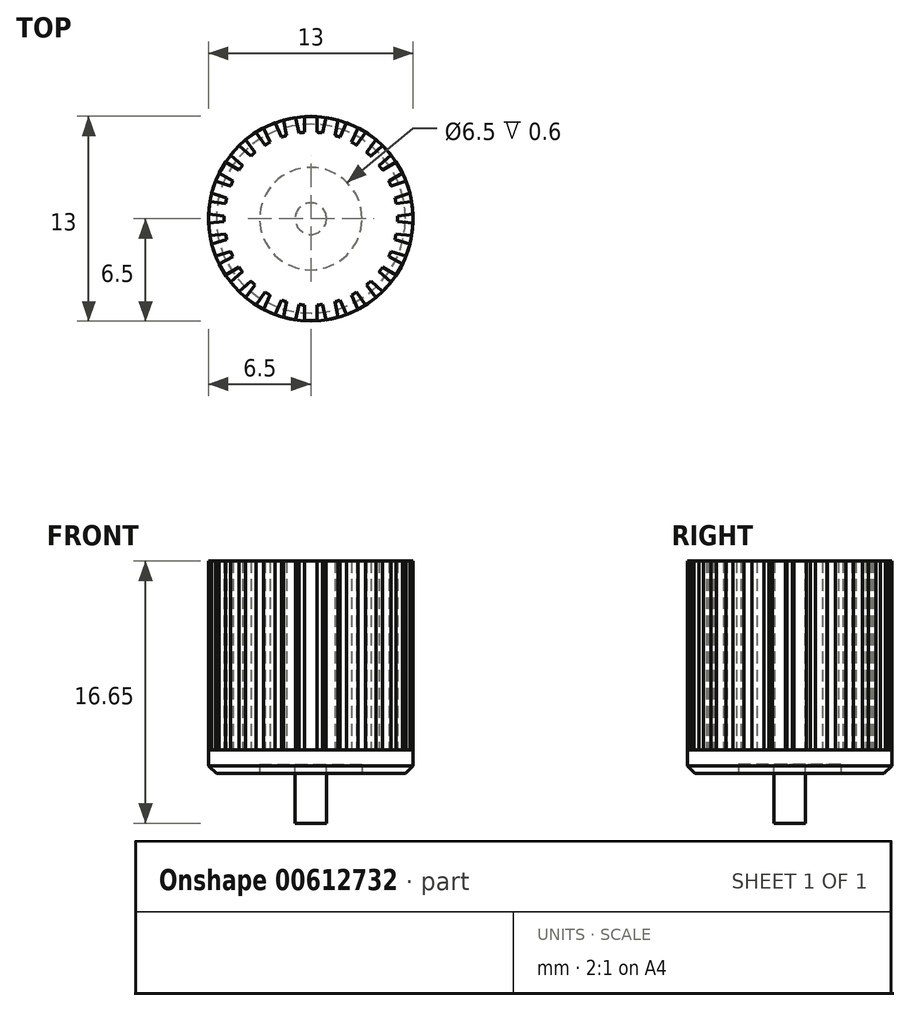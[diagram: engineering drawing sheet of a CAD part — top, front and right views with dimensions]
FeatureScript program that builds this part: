
annotation { "Feature Type Name" : "Feature", "Feature Type Description" : "" }
export const myFeature = defineFeature(function(context is Context, id is Id, definition is map)
    precondition{}
    {
        {
            var Q0;
            Q0=qCreatedBy(makeId("Top.planeOp"),FACE);
            var sketch = newSketch(context, id + "F0", { "sketchPlane" : qUnion([Q0])});
            skCircle(sketch, "E0", {"center": v(0, 0) * mm, "radius": 5.5 * mm});
            skSolve(sketch);
        }
        {
            var Q0;
            Q0=qSketchRegion(id+"F0",true);
            extrude(context, id + "F1", {"entities" : qUnion([Q0]), "depth" : 12 * mm, "offsetDistance" : 25 * mm});
        }
        {
            var Q0;
            Q0=qCreatedBy(makeId("Top.planeOp"),FACE);
            var sketch = newSketch(context, id + "F2", { "sketchPlane" : qUnion([Q0])});
            skArc(sketch, "E1.0", {"start": v(0.4, 5.49) * mm, "mid": v(0, 5.5) * mm, "end": v(-0.4, 5.49) * mm});
            skLineSegment(sketch, "E2", {"start": v(-0.4, 5.49) * mm, "end": v(-0.4, 6.49) * mm});
            skLineSegment(sketch, "E3", {"start": v(-0.4, 6.49) * mm, "end": v(0.4, 6.49) * mm});
            skLineSegment(sketch, "E4", {"start": v(0.4, 6.49) * mm, "end": v(0.4, 5.49) * mm});
            skSolve(sketch);
        }
        {
            var Q0;
            Q0=qSketchRegion(id+"F2",true);
            extrude(context, id + "F3", {"entities" : qUnion([Q0]), "depth" : 12 * mm, "offsetDistance" : 25 * mm});
        }
        {
            var Q0;
            Q0=makeQuery(id+"F3.opExtrude","SWEPT_BODY",BODY,{"disambiguationData":[OSD([sQuery(id+"F2.wireOp",EDGE,"E1.0"),sQuery(id+"F2.wireOp",EDGE,"E2"),sQuery(id+"F2.wireOp",EDGE,"E3"),sQuery(id+"F2.wireOp",EDGE,"E4")])]});
            var Q1;
            Q1=makeQuery(id+"F1.opExtrude","CAP_EDGE",EDGE,{"disambiguationData":[OSD([sQuery(id+"F0.wireOp",EDGE,"E0")])],"isStart":false});
            circularPattern(context, id + "F4", {"entities" : qUnion([Q0]), "axis" : qUnion([Q1]), "angle" : 360 * degree, "instanceCount" : 30, "equalSpace" : true});
        }
        {
            var Q0;
            Q0=qCreatedBy(makeId("Top.planeOp"),FACE);
            var sketch = newSketch(context, id + "F5", { "sketchPlane" : qUnion([Q0])});
            skCircle(sketch, "E5", {"center": v(0, 0) * mm, "radius": 6.5 * mm});
            skSolve(sketch);
        }
        {
            var Q0;
            Q0=qSketchRegion(id+"F5",true);
            extrude(context, id + "F6", {"entities" : qUnion([Q0]), "operationType" : NewBodyOperationType.ADD, "oppositeDirection" : true, "depth" : 1.5 * mm, "offsetDistance" : 25 * mm});
        }
        {
            var Q0;
            Q0=makeQuery(id+"F6.opExtrude","CAP_EDGE",EDGE,{"disambiguationData":[OSD([sQuery(id+"F5.wireOp",EDGE,"E5")])],"isStart":false});
            chamfer(context, id + "F7", {"entities" : qUnion([Q0]), "width" : 0.5 * mm, "tangentPropagation" : true});
        }
        {
            var Q0;
            Q0=makeQuery(id+"F6.opExtrude","CAP_FACE",FACE,{"disambiguationData":[OSD([sQuery(id+"F5.wireOp",EDGE,"E5")])],"isStart":false});
            var sketch = newSketch(context, id + "F8", { "sketchPlane" : qUnion([Q0])});
            skCircle(sketch, "E6", {"center": v(0, 0) * mm, "radius": 3.25 * mm});
            skSolve(sketch);
        }
        {
            var Q0;
            Q0=qSketchRegion(id+"F8",true);
            extrude(context, id + "F9", {"entities" : qUnion([Q0]), "operationType" : NewBodyOperationType.REMOVE, "oppositeDirection" : true, "depth" : 0.6 * mm, "offsetDistance" : 25 * mm});
        }
        {
            var Q0;
            Q0=makeQuery(id+"F9.boolean.opBoolean","COPY",FACE,{"derivedFrom":makeQuery(id+"F9.opExtrude","CAP_FACE",FACE,{"disambiguationData":[OSD([sQuery(id+"F8.wireOp",EDGE,"E6")])],"isStart":false})});
            var sketch = newSketch(context, id + "F10", { "sketchPlane" : qUnion([Q0])});
            skCircle(sketch, "E7", {"center": v(0, 0) * mm, "radius": 1 * mm});
            skSolve(sketch);
        }
        {
            var Q0;
            Q0=qSketchRegion(id+"F10",true);
            extrude(context, id + "F11", {"entities" : qUnion([Q0]), "operationType" : NewBodyOperationType.ADD, "depth" : 3.75 * mm, "offsetDistance" : 25 * mm});
        }
    });
